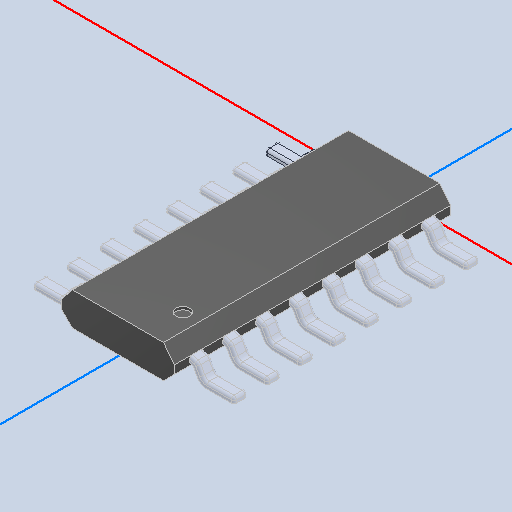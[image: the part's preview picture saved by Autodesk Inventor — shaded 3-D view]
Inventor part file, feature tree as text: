
AUTODESK INVENTOR PART (.ipt)
format: ipt  version: 2022 (Build 260153000, 153)  size: 644,608 bytes
history: native  units: mm
features: other x25, mirror x8, fillet x1
ambient origin geometry x8: Origin, YZ Plane, XZ Plane, XY Plane, X Axis, Y Axis, Z Axis, Center Point
bodies: Body1 (feature_tree), Body2 (feature_tree), Body3 (feature_tree), Body4 (feature_tree), Body5 (feature_tree), Body6 (feature_tree), Body7 (feature_tree), Body8 (feature_tree), Body9 (feature_tree), Body10 (feature_tree), Body11 (feature_tree), Body12 (feature_tree), Body13 (feature_tree), Body14 (feature_tree), Body15 (feature_tree), Body16 (feature_tree), Body17 (feature_tree)
feature tree (34):
  other  "Твердое тело1"
  other  "Твердое тело2"
  other  "Твердое тело3"
  other  "Твердое тело4"
  other  "Твердое тело5"
  other  "Твердое тело6"
  other  "Твердое тело7"
  other  "Твердое тело8"
  other  "Твердое тело9"
  other  "Твердое тело10"
  other  "Твердое тело11"
  other  "Твердое тело12"
  other  "Твердое тело13"
  other  "Твердое тело14"
  other  "Твердое тело15"
  other  "Твердое тело16"
  other  "Твердое тело17"
  fillet  "Fillet1"  [1 undecoded]
  other  "LPattern1[1]"
  other  "LPattern1[2]"
  other  "LPattern1[3]"
  mirror  "Mirror1[1]"
  mirror  "Mirror1[2]"
  mirror  "Mirror1[3]"
  mirror  "Mirror1[4]"
  other  "LPattern1[4]"
  other  "LPattern1[5]"
  other  "LPattern1[6]"
  mirror  "Mirror1[5]"
  mirror  "Mirror1[6]"
  mirror  "Mirror1[7]"
  other  "Cut-Extrude1"
  other  "LPattern1[7]"
  mirror  "Mirror1[8]"
note: 1 required parameter value undecoded (feature->parameter linkage not recoverable at this tier; creation-order binding heuristic only, values carry confidence <= 0.55)
